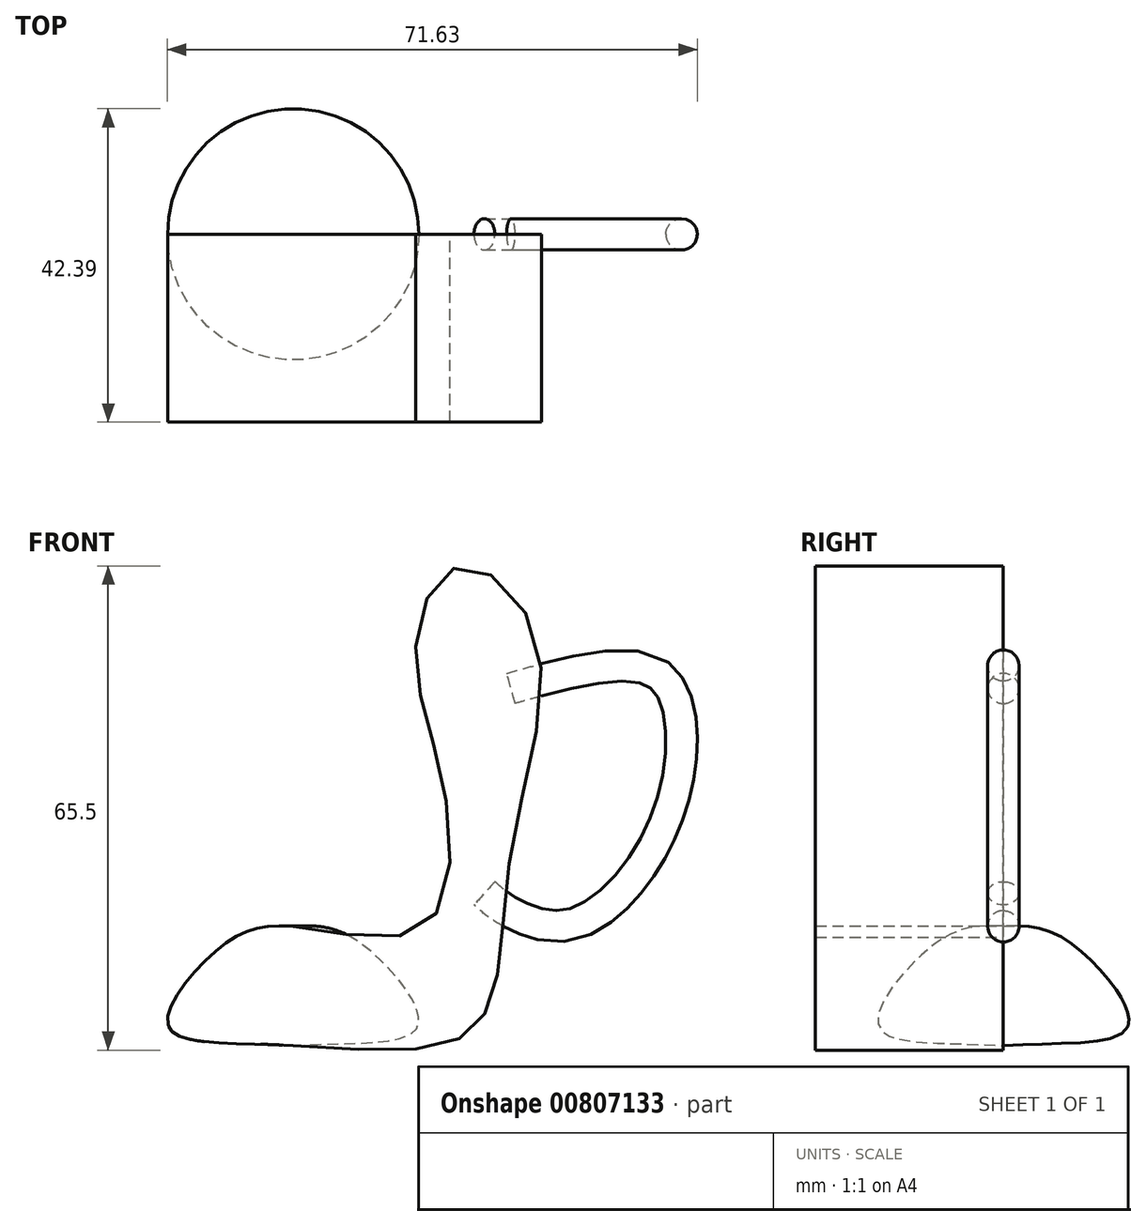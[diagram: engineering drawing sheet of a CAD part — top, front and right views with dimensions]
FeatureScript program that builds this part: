
annotation { "Feature Type Name" : "Feature", "Feature Type Description" : "" }
export const myFeature = defineFeature(function(context is Context, id is Id, definition is map)
    precondition{}
    {
        {
            var Q0;
            Q0=qCreatedBy(makeId("Front.planeOp"),FACE);
            var sketch = newSketch(context, id + "F0", { "sketchPlane" : qUnion([Q0])});
            skFitSpline(sketch, "E0", {"points": [v(0, 0) * mm, v(-10.11, -3.03) * mm, v(-16.9, -13.36) * mm, v(-2.92, -15.98) * mm, v(20.8, -15.83) * mm, v(26.94, -9.38) * mm, v(29.58, 10.95) * mm, v(32.74, 39.48) * mm, v(22.26, 48.67) * mm, v(16.58, 37.6) * mm, v(20.23, 19.61) * mm, v(17.74, 0) * mm, v(0, 0) * mm]});
            skLineSegment(sketch, "E1", {"start": v(0, 55.19) * mm, "end": v(0, -37.96) * mm});
            skSolve(sketch);
        }
        {
            var Q0;
            Q0=qCreatedBy(makeId("Front.planeOp"),FACE);
            var sketch = newSketch(context, id + "F1", { "sketchPlane" : qUnion([Q0])});
            skLineSegment(sketch, "E2", {"start": v(0, 76) * mm, "end": v(0, -76.57) * mm});
            skSolve(sketch);
        }
        {
            var Q0;
            {var subQ0=sQuery(id+"F0.wireOp",EDGE,"E1");var subQ1=sQuery(id+"F0.wireOp",EDGE,"E0");var subQ2=makeQuery(id+"F0.imprint","INTERSECT",VERTEX,{"disambiguationData":[OD(0.0)],"derivedFrom":[subQ1,subQ0]});Q0=makeQuery(id+"F0.imprint","IMPRINT",FACE,{"disambiguationData":[TD([[makeQuery(id+"F0.imprint","IMPRINT",EDGE,{"disambiguationData":[TD([[subQ2,-1.0]])],"derivedFrom":subQ1}),1.0]])]});}
            var Q1;
            Q1=sQuery(id+"F1.wireOp",EDGE,"E2");
            revolve(context, id + "F2", {"surfaceOperationType" : NewSurfaceOperationType.NEW, "entities" : qUnion([Q0]), "axis" : qUnion([Q1]), "revolveType" : RevolveType.FULL});
        }
        {
            var Q0;
            Q0=qCreatedBy(makeId("Front.planeOp"),FACE);
            var sketch = newSketch(context, id + "F3", { "sketchPlane" : qUnion([Q0])});
            skFitSpline(sketch, "E3", {"points": [v(29.4, 32.34) * mm, v(49.17, 34.39) * mm, v(52.58, 23.48) * mm, v(47.35, 8.26) * mm, v(36.9, 0) * mm, v(28.72, 2.13) * mm, v(25.77, 4.4) * mm], "startDerivative": vector(108.23, 30.7) * mm, "endDerivative": vector(-25.86, 23.15) * mm});
            skSolve(sketch);
        }
        {
            var Q0;
            Q0=sQuery(id+"F3.wireOp",EDGE,"E3");
            var Q1;
            Q1=sQuery(id+"F3.wireOp",VERTEX,"E3.end");
            cPlane(context, id + "F4", {"entities" : qUnion([Q0, Q1]), "cplaneType" : CPlaneType.CURVE_POINT, "offset" : 25.4 * mm, "width" : 152.4 * mm, "height" : 152.4 * mm});
        }
        {
            var Q0;
            Q0=qCreatedBy(id+"F4.planeOp",FACE);
            var sketch = newSketch(context, id + "F5", { "sketchPlane" : qUnion([Q0])});
            skCircle(sketch, "E4", {"center": v(0, 20.6) * mm, "radius": 2.12 * mm});
            skSolve(sketch);
        }
        {
            var Q0;
            Q0=makeQuery(id+"F5.imprint","IMPRINT",FACE,{"disambiguationData":[TD([[makeQuery(id+"F5.imprint","IMPRINT",EDGE,{"derivedFrom":sQuery(id+"F5.wireOp",EDGE,"E4")}),1.0]])]});
            var Q1;
            Q1=sQuery(id+"F3.wireOp",EDGE,"E3");
            sweep(context, id + "F6", {"profiles" : qUnion([Q0]), "path" : qUnion([Q1])});
        }
        {
            var Q0;
            Q0=makeQuery(id+"F0.imprint","IMPRINT",FACE,{"disambiguationData":[TD([[makeQuery(id+"F0.imprint","IMPRINT",EDGE,{"derivedFrom":sQuery(id+"F0.wireOp",EDGE,"E0")}),1.0]])]});
            extrude(context, id + "F7", {"entities" : qUnion([Q0]), "depth" : 25.4 * mm, "offsetDistance" : 25.4 * mm});
        }
    });
